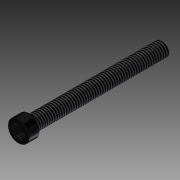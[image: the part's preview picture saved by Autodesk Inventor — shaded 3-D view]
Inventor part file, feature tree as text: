
AUTODESK INVENTOR PART (.ipt)
format: ipt  version: 2013 (Build 170138000, 138)  size: 106,496 bytes
history: native  units: in
note: dims shown in document units (in); Inventor stores cm internally (conversion verified against a paired STEP export)
features: extrude x3, sketch x1, thread x1, chamfer x1
ambient origin geometry x8: Origin, YZ Plane, XZ Plane, XY Plane, X Axis, Y Axis, Z Axis, Center Point
bodies: Solid1 (feature_tree)
feature tree (6):
  sketch  "Sketch1"  dims[d0=0.275in d1=0.185in d2=0.15in d3=0.15in d4=0.0in d5=1.715in d6=0.0in d7=0.05in d8=0.0in d9=1.0in d10=0.0in d11=0.01in d12=0.125in d13=45.0deg]
  extrude  "Extrusion1"  Depth=0.185in
  extrude  "Extrusion2"  Depth=0.15in
  extrude  "Extrusion3"  Depth=0.15in TaperAngle=0.0deg
  thread  "Thread1"  [1 undecoded]
  chamfer  "Chamfer1"  Distance=0.05in
note: 1 required parameter value undecoded (feature->parameter linkage not recoverable at this tier; creation-order binding heuristic only, values carry confidence <= 0.55)
